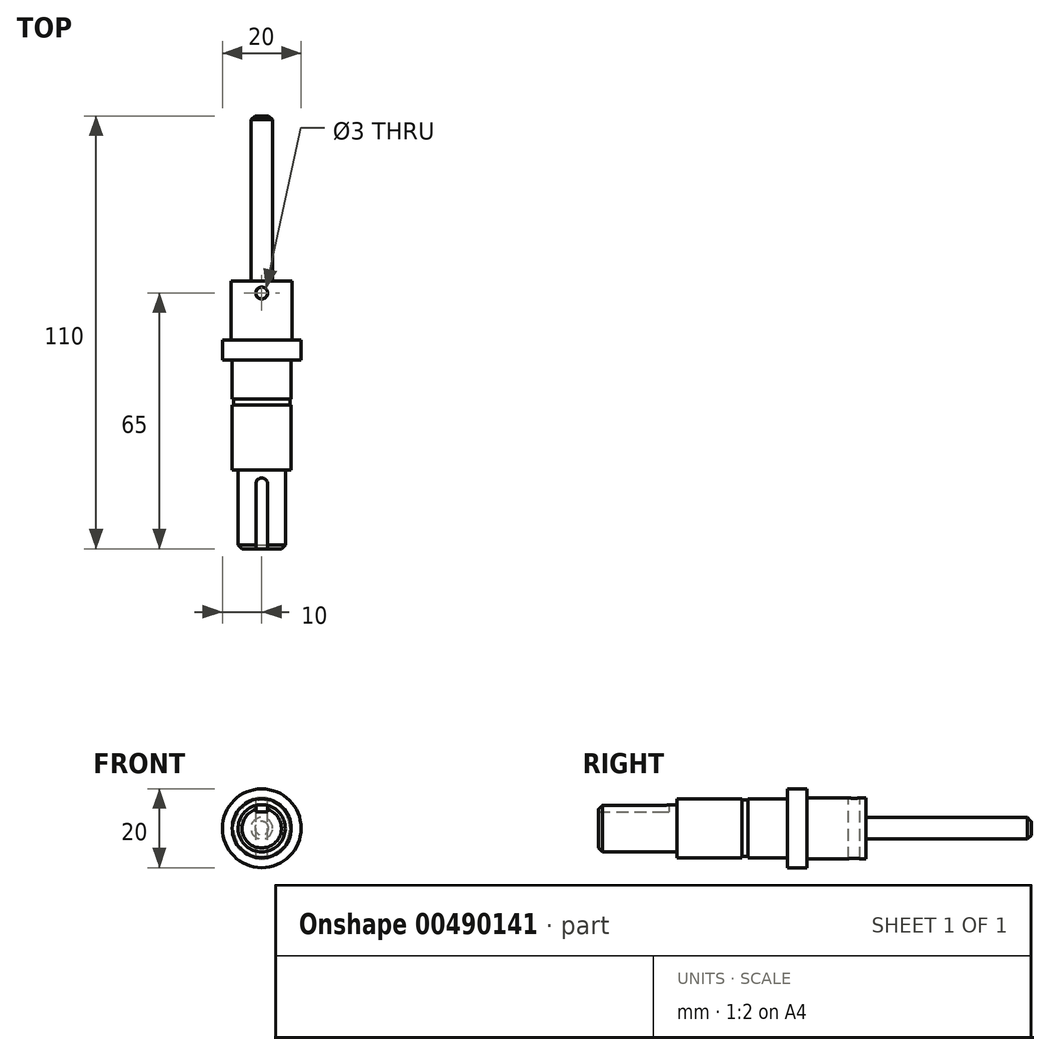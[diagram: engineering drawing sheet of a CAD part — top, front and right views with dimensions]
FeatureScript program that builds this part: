
annotation { "Feature Type Name" : "Feature", "Feature Type Description" : "" }
export const myFeature = defineFeature(function(context is Context, id is Id, definition is map)
    precondition{}
    {
        {
            var Q0;
            Q0=qCreatedBy(makeId("Front.planeOp"),FACE);
            var sketch = newSketch(context, id + "F0", { "sketchPlane" : qUnion([Q0])});
            skCircle(sketch, "E0", {"center": v(0, 0) * mm, "radius": 10 * mm});
            skSolve(sketch);
        }
        {
            var Q0;
            Q0 = qSketchRegion(id + "F0", true);
            extrude(context, id + "F1", {"entities" : qUnion([Q0]), "endBound" : BoundingType.SYMMETRIC, "depth" : 5 * mm});
        }
        {
            var Q0;
            Q0=makeQuery(id+"F1.opExtrude","CAP_FACE",FACE,{"disambiguationData":[OSD([sQuery(id+"F0.wireOp",EDGE,"E0")])],"isStart":false});
            var sketch = newSketch(context, id + "F2", { "sketchPlane" : qUnion([Q0])});
            skCircle(sketch, "E1", {"center": v(0, 0) * mm, "radius": 7.5 * mm});
            skSolve(sketch);
        }
        {
            var Q0;
            Q0 = qSketchRegion(id + "F2", true);
            extrude(context, id + "F3", {"entities" : qUnion([Q0]), "operationType" : NewBodyOperationType.ADD, "depth" : 10 * mm});
        }
        {
            var Q0;
            Q0=makeQuery(id+"F3.opExtrude","CAP_FACE",FACE,{"disambiguationData":[OSD([sQuery(id+"F2.wireOp",EDGE,"E1")])],"isStart":false});
            var sketch = newSketch(context, id + "F4", { "sketchPlane" : qUnion([Q0])});
            skCircle(sketch, "E2", {"center": v(0, 0) * mm, "radius": 7.15 * mm});
            skSolve(sketch);
        }
        {
            var Q0;
            Q0 = qSketchRegion(id + "F4", true);
            extrude(context, id + "F5", {"entities" : qUnion([Q0]), "operationType" : NewBodyOperationType.ADD, "depth" : 1.5 * mm});
        }
        {
            var Q0;
            Q0=makeQuery(id+"F5.opExtrude","CAP_FACE",FACE,{"disambiguationData":[OSD([sQuery(id+"F4.wireOp",EDGE,"E2")])],"isStart":false});
            var sketch = newSketch(context, id + "F6", { "sketchPlane" : qUnion([Q0])});
            skCircle(sketch, "E3", {"center": v(0, 0) * mm, "radius": 7.5 * mm});
            skSolve(sketch);
        }
        {
            var Q0;
            Q0 = qSketchRegion(id + "F6", true);
            extrude(context, id + "F7", {"entities" : qUnion([Q0]), "operationType" : NewBodyOperationType.ADD, "depth" : 16.5 * mm});
        }
        {
            var Q0;
            Q0=makeQuery(id+"F7.opExtrude","CAP_FACE",FACE,{"disambiguationData":[OSD([sQuery(id+"F6.wireOp",EDGE,"E3")])],"isStart":false});
            var sketch = newSketch(context, id + "F8", { "sketchPlane" : qUnion([Q0])});
            skCircle(sketch, "E4", {"center": v(0, 0) * mm, "radius": 6 * mm});
            skSolve(sketch);
        }
        {
            var Q0;
            Q0 = qSketchRegion(id + "F8", true);
            extrude(context, id + "F9", {"entities" : qUnion([Q0]), "operationType" : NewBodyOperationType.ADD, "depth" : 20 * mm});
        }
        {
            var Q0;
            Q0=makeQuery(id+"F9.opExtrude","CAP_EDGE",EDGE,{"disambiguationData":[OSD([sQuery(id+"F8.wireOp",EDGE,"E4")])],"isStart":false});
            chamfer(context, id + "F10", {"entities" : qUnion([Q0]), "width" : 1 * mm, "tangentPropagation" : true});
        }
        {
            var Q0;
            Q0=makeQuery(id+"F1.opExtrude","CAP_FACE",FACE,{"disambiguationData":[OSD([sQuery(id+"F0.wireOp",EDGE,"E0")])],"isStart":true});
            var sketch = newSketch(context, id + "F11", { "sketchPlane" : qUnion([Q0])});
            skCircle(sketch, "E5", {"center": v(0, 0) * mm, "radius": 7.75 * mm});
            skSolve(sketch);
        }
        {
            var Q0;
            Q0 = qSketchRegion(id + "F11", true);
            extrude(context, id + "F12", {"entities" : qUnion([Q0]), "operationType" : NewBodyOperationType.ADD, "depth" : 15 * mm});
        }
        {
            var Q0;
            Q0=makeQuery(id+"F12.opExtrude","CAP_FACE",FACE,{"disambiguationData":[OSD([sQuery(id+"F11.wireOp",EDGE,"E5")])],"isStart":false});
            var sketch = newSketch(context, id + "F13", { "sketchPlane" : qUnion([Q0])});
            skCircle(sketch, "E6", {"center": v(0, 0) * mm, "radius": 2.75 * mm});
            skSolve(sketch);
        }
        {
            var Q0;
            Q0 = qSketchRegion(id + "F13", true);
            extrude(context, id + "F14", {"entities" : qUnion([Q0]), "operationType" : NewBodyOperationType.ADD, "depth" : 42 * mm});
        }
        {
            var Q0;
            Q0=makeQuery(id+"F14.opExtrude","CAP_EDGE",EDGE,{"disambiguationData":[OSD([sQuery(id+"F13.wireOp",EDGE,"E6")])],"isStart":false});
            chamfer(context, id + "F15", {"entities" : qUnion([Q0]), "width" : 1 * mm, "tangentPropagation" : true});
        }
        {
            var Q0;
            Q0=qCreatedBy(makeId("Top.planeOp"),FACE);
            var sketch = newSketch(context, id + "F16", { "sketchPlane" : qUnion([Q0])});
            skCircle(sketch, "E7", {"center": v(0, 14.5) * mm, "radius": 1.5 * mm});
            skSolve(sketch);
        }
        {
            var Q0;
            Q0 = qSketchRegion(id + "F16", true);
            extrude(context, id + "F17", {"entities" : qUnion([Q0]), "operationType" : NewBodyOperationType.REMOVE, "endBound" : BoundingType.SYMMETRIC, "oppositeDirection" : true, "depth" : 25 * mm});
        }
        {
            var Q0;
            Q0=qCreatedBy(makeId("Top.planeOp"),FACE);
            var sketch = newSketch(context, id + "F18", { "sketchPlane" : qUnion([Q0])});
            skLineSegment(sketch, "E8.bottom", {"start": v(-1.5, -50.5) * mm, "end": v(1.5, -50.5) * mm});
            skLineSegment(sketch, "E8.top", {"start": v(0, -32.5) * mm, "end": v(0, -32.5) * mm});
            skLineSegment(sketch, "E8.left", {"start": v(-1.5, -50.5) * mm, "end": v(-1.5, -34) * mm});
            skLineSegment(sketch, "E8.right", {"start": v(1.5, -50.5) * mm, "end": v(1.5, -34) * mm});
            skPoint(sketch, "E9.visualSharp", {"position": v(-1.5, -32.5) * mm});
            skArc(sketch, "E9.filletArc", {"start": v(0, -32.5) * mm, "mid": v(-1.06, -32.94) * mm, "end": v(-1.5, -34) * mm});
            skPoint(sketch, "E10.visualSharp", {"position": v(1.5, -32.5) * mm});
            skArc(sketch, "E10.filletArc", {"start": v(1.5, -34) * mm, "mid": v(1.06, -32.94) * mm, "end": v(0, -32.5) * mm});
            skSolve(sketch);
        }
        {
            var Q0;
            Q0 = qSketchRegion(id + "F18", true);
            extrude(context, id + "F19", {"entities" : qUnion([Q0]), "operationType" : NewBodyOperationType.REMOVE, "depth" : 6 * mm});
        }
        {
            var Q0;
            Q0 = qSketchRegion(id + "F18", true);
            extrude(context, id + "F20", {"entities" : qUnion([Q0]), "operationType" : NewBodyOperationType.ADD, "depth" : 4.2 * mm});
        }
    });
